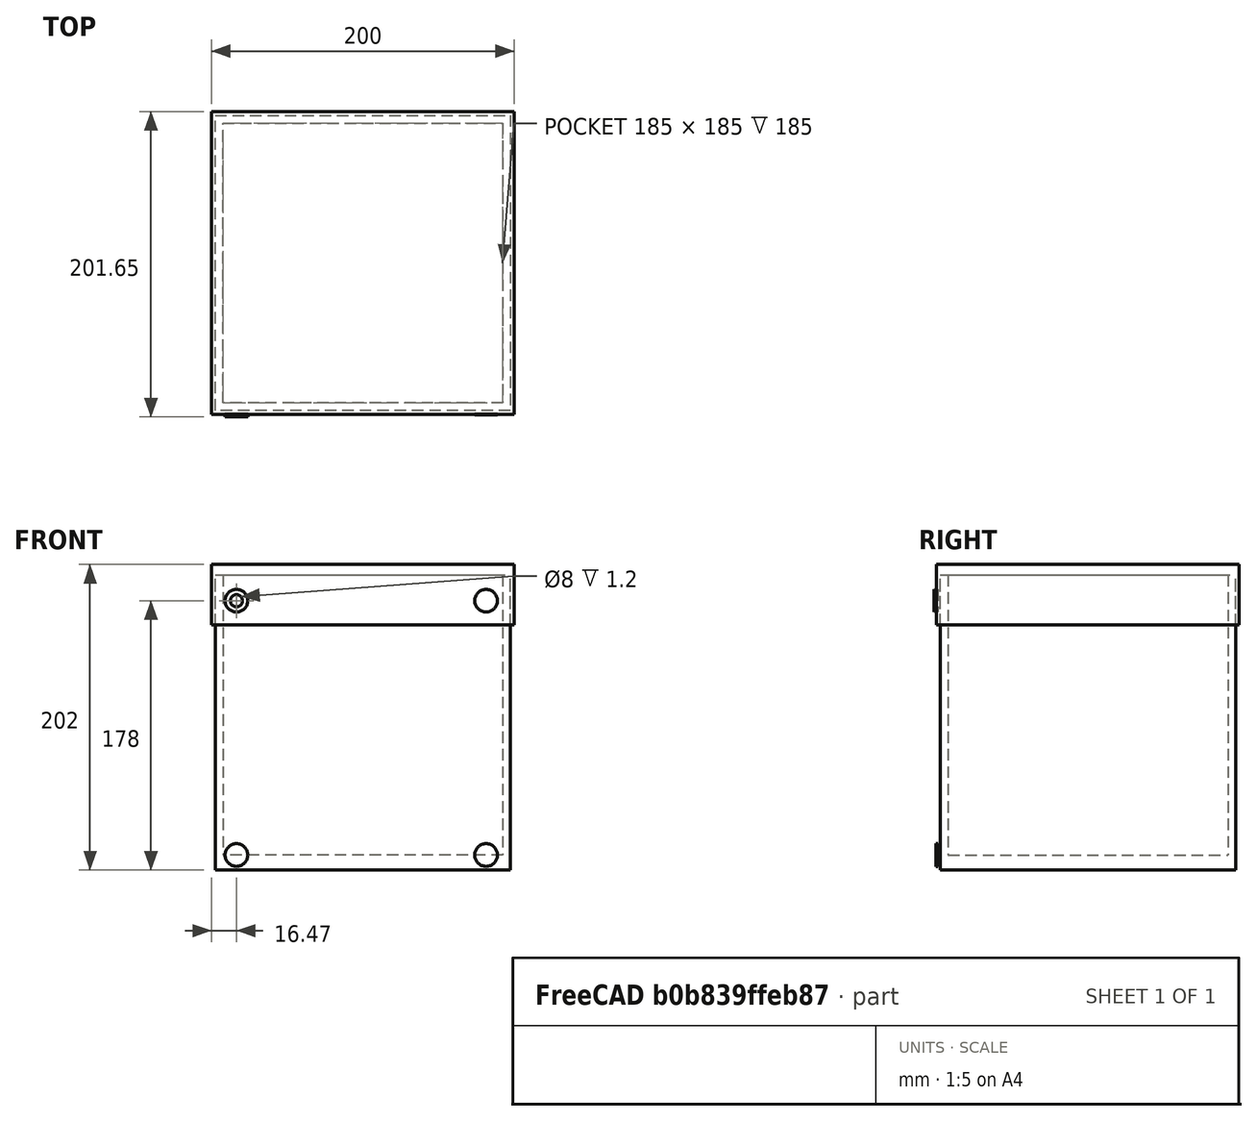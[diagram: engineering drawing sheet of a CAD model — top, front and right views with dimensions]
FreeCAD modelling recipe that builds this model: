
FCSTD DOCUMENT  (FreeCAD 0.20R)
Label: box_assembly
License: All rights reserved
LicenseURL: http://en.wikipedia.org/wiki/All_rights_reserved
objects: Sketcher::SketchObject×8, PartDesign::Pad×6, PartDesign::Body×6, Mesh::Feature×4, PartDesign::Pocket×2
note: 30 computed .brp shape members not serialized (recipe doc carries the construction recipe); baked Part::Feature solids carry a one-line shape summary decoded from their .brp

FEATURE [Sketcher::SketchObject] Sketch
  FullyConstrained = true
  MapMode = 5
  Support = -> [XY_Plane]
  sketch-geometry (4):
    g0: LineSegment StartX=-97.5 StartY=97.5 StartZ=0 EndX=97.5 EndY=97.5 EndZ=0
    g1: LineSegment StartX=97.5 StartY=97.5 StartZ=0 EndX=97.5 EndY=-97.5 EndZ=0
    g2: LineSegment StartX=97.5 StartY=-97.5 StartZ=0 EndX=-97.5 EndY=-97.5 EndZ=0
    g3: LineSegment StartX=-97.5 StartY=-97.5 StartZ=0 EndX=-97.5 EndY=97.5 EndZ=0
  constraints (11):
    c: Coincident(g0,g1)
    c: Coincident(g1,g2)
    c: Coincident(g2,g3)
    c: Coincident(g3,g0)
    c: Horizontal(g0)
    c: Horizontal(g2)
    c: Vertical(g1)
    c: Vertical(g3)
    c: DistanceX(g0,g0) = 195
    c: DistanceY(g1,g1) = 195
    c: Symmetric(g1,g0,g-1)
FEATURE [PartDesign::Pad] Pad
  Direction = (0,0,1)
  Length = 195
  Length2 = 10
  Profile = -> Sketch
  ReferenceAxis = -> Sketch [N_Axis]
  Type = 0
FEATURE [Sketcher::SketchObject] Sketch001
  FullyConstrained = true
  MapMode = 5
  Placement = pos=(0,0,195) rot=(0,0,1;0rad)
  Support = -> [Pad]
  sketch-geometry (4):
    g0: LineSegment StartX=-92.5 StartY=92.5 StartZ=0 EndX=92.5 EndY=92.5 EndZ=0
    g1: LineSegment StartX=92.5 StartY=92.5 StartZ=0 EndX=92.5 EndY=-92.5 EndZ=0
    g2: LineSegment StartX=92.5 StartY=-92.5 StartZ=0 EndX=-92.5 EndY=-92.5 EndZ=0
    g3: LineSegment StartX=-92.5 StartY=-92.5 StartZ=0 EndX=-92.5 EndY=92.5 EndZ=0
  constraints (11):
    c: Coincident(g0,g1)
    c: Coincident(g1,g2)
    c: Coincident(g2,g3)
    c: Coincident(g3,g0)
    c: Horizontal(g0)
    c: Horizontal(g2)
    c: Vertical(g1)
    c: Vertical(g3)
    c: DistanceX(g0,g0) = 185
    c: DistanceY(g1,g1) = 185
    c: Symmetric(g0,g1,g-1)
FEATURE [PartDesign::Pocket] Pocket
  BaseFeature = -> Pad
  Direction = (0,0,-1)
  Length = 185
  Length2 = 5
  Profile = -> Sketch001
  ReferenceAxis = -> Sketch001 [N_Axis]
  Type = 0
FEATURE [PartDesign::Body] Body  label="Box"
  Group = -> [Sketch,Pad,Sketch001,Pocket]
  Origin = -> Origin
  Tip = -> Pocket
FEATURE [Sketcher::SketchObject] Sketch002
  FullyConstrained = true
  MapMode = 5
  Support = -> [XY_Plane001]
  sketch-geometry (1):
    g0: Circle CenterX=0 CenterY=0 CenterZ=0 NormalX=0 NormalY=0 NormalZ=1 AngleXU=0 Radius=7.5
  constraints (2):
    c: Coincident(g0,g-1)
    c: Diameter(g0) = 15
FEATURE [PartDesign::Pad] Pad001
  Direction = (0,0,1)
  Length = 2.4
  Length2 = 10
  Profile = -> Sketch002
  ReferenceAxis = -> Sketch002 [N_Axis]
  Type = 0
FEATURE [Sketcher::SketchObject] Sketch003
  FullyConstrained = true
  MapMode = 5
  Support = -> [XY_Plane002]
  sketch-geometry (1):
    g0: Circle CenterX=0 CenterY=0 CenterZ=0 NormalX=0 NormalY=0 NormalZ=1 AngleXU=0 Radius=7.5
  constraints (2):
    c: Coincident(g0,g-1)
    c: Diameter(g0) = 15
FEATURE [PartDesign::Pad] Pad002
  Direction = (0,0,1)
  Length = 1.2
  Length2 = 10
  Profile = -> Sketch003
  ReferenceAxis = -> Sketch003 [N_Axis]
  Type = 0
FEATURE [PartDesign::Body] Body002  label="box_dot001"
  Group = -> [Sketch003,Pad002]
  Origin = -> Origin002
  Placement = pos=(81.4701,-99.2518,178) rot=(0.57735,-0.57735,0.57735;2.0944rad)
  Tip = -> Pad002
FEATURE [Sketcher::SketchObject] Sketch004
  FullyConstrained = true
  MapMode = 5
  Support = -> [XY_Plane003]
  sketch-geometry (1):
    g0: Circle CenterX=0 CenterY=0 CenterZ=0 NormalX=0 NormalY=0 NormalZ=1 AngleXU=0 Radius=7.5
  constraints (2):
    c: Coincident(g0,g-1)
    c: Diameter(g0) = 15
FEATURE [PartDesign::Pad] Pad003
  Direction = (0,0,1)
  Length = 1.2
  Length2 = 10
  Profile = -> Sketch004
  ReferenceAxis = -> Sketch004 [N_Axis]
  Type = 0
FEATURE [PartDesign::Body] Body003  label="box_dot002"
  Group = -> [Sketch004,Pad003]
  Origin = -> Origin003
  Placement = pos=(81.4701,-99.2518,10) rot=(0.57735,-0.57735,0.57735;2.0944rad)
  Tip = -> Pad003
FEATURE [Sketcher::SketchObject] Sketch005
  FullyConstrained = true
  MapMode = 5
  Support = -> [XY_Plane004]
  sketch-geometry (1):
    g0: Circle CenterX=0 CenterY=0 CenterZ=0 NormalX=0 NormalY=0 NormalZ=1 AngleXU=0 Radius=7.5
  constraints (2):
    c: Coincident(g0,g-1)
    c: Diameter(g0) = 15
FEATURE [PartDesign::Pad] Pad004
  Direction = (0,0,1)
  Length = 1.2
  Length2 = 10
  Profile = -> Sketch005
  ReferenceAxis = -> Sketch005 [N_Axis]
  Type = 0
FEATURE [PartDesign::Body] Body004  label="box_dot003"
  Group = -> [Sketch005,Pad004]
  Origin = -> Origin004
  Placement = pos=(-83.5299,-99.2518,10) rot=(0.57735,-0.57735,0.57735;2.0944rad)
  Tip = -> Pad004
FEATURE [Sketcher::SketchObject] Sketch006
  FullyConstrained = true
  MapMode = 5
  Support = -> [XY_Plane005]
  sketch-geometry (4):
    g0: LineSegment StartX=-100 StartY=100 StartZ=0 EndX=100 EndY=100 EndZ=0
    g1: LineSegment StartX=100 StartY=100 StartZ=0 EndX=100 EndY=-100 EndZ=0
    g2: LineSegment StartX=100 StartY=-100 StartZ=0 EndX=-100 EndY=-100 EndZ=0
    g3: LineSegment StartX=-100 StartY=-100 StartZ=0 EndX=-100 EndY=100 EndZ=0
  constraints (11):
    c: Coincident(g0,g1)
    c: Coincident(g1,g2)
    c: Coincident(g2,g3)
    c: Coincident(g3,g0)
    c: Horizontal(g0)
    c: Horizontal(g2)
    c: Vertical(g1)
    c: Vertical(g3)
    c: DistanceX(g0,g0) = 200
    c: DistanceY(g3,g3) = 200
    c: Symmetric(g0,g2,g-1)
FEATURE [PartDesign::Pad] Pad005
  Direction = (0,0,1)
  Length = 40
  Length2 = 10
  Profile = -> Sketch006
  ReferenceAxis = -> Sketch006 [N_Axis]
  Type = 0
FEATURE [PartDesign::Body] Body005  label="Lid"
  Group = -> [Sketch006,Pad005]
  Origin = -> Origin005
  Placement = pos=(-2.5e-14,0,202) rot=(0,1,0;3.14159rad)
  Tip = -> Pad005
FEATURE [Mesh::Feature] star
  Placement = pos=(0.172088,99.5226,81.3081) rot=(0,-0.707107,-0.707107;3.14159rad)
FEATURE [Mesh::Feature] feather
  Placement = pos=(97,69,14) rot=(0.57735,0.57735,0.57735;2.0944rad)
FEATURE [Mesh::Feature] flower
  Placement = pos=(70,-97,16) rot=(1,0,0;1.5708rad)
FEATURE [Mesh::Feature] mushroom
  Placement = pos=(-104,-117,10) rot=(0.57735,-0.57735,-0.57735;2.0944rad)
FEATURE [Sketcher::SketchObject] Sketch007
  FullyConstrained = true
  MapMode = 5
  Placement = pos=(0,0,2.4) rot=(0,0,1;0rad)
  Support = -> [Pad001]
  sketch-geometry (1):
    g0: Circle CenterX=0 CenterY=0 CenterZ=0 NormalX=0 NormalY=0 NormalZ=1 AngleXU=0 Radius=4
  constraints (2):
    c: Coincident(g0,g-1)
    c: Diameter(g0) = 8
FEATURE [PartDesign::Pocket] Pocket001
  BaseFeature = -> Pad001
  Direction = (0,0,-1)
  Length = 1.2
  Length2 = 5
  Profile = -> Sketch007
  ReferenceAxis = -> Sketch007 [N_Axis]
  Type = 0
FEATURE [PartDesign::Body] Body001  label="box_dot"
  Group = -> [Sketch002,Pad001,Sketch007,Pocket001]
  Origin = -> Origin001
  Placement = pos=(-83.5299,-99.2518,178) rot=(0.57735,-0.57735,0.57735;2.0944rad)
  Tip = -> Pocket001
